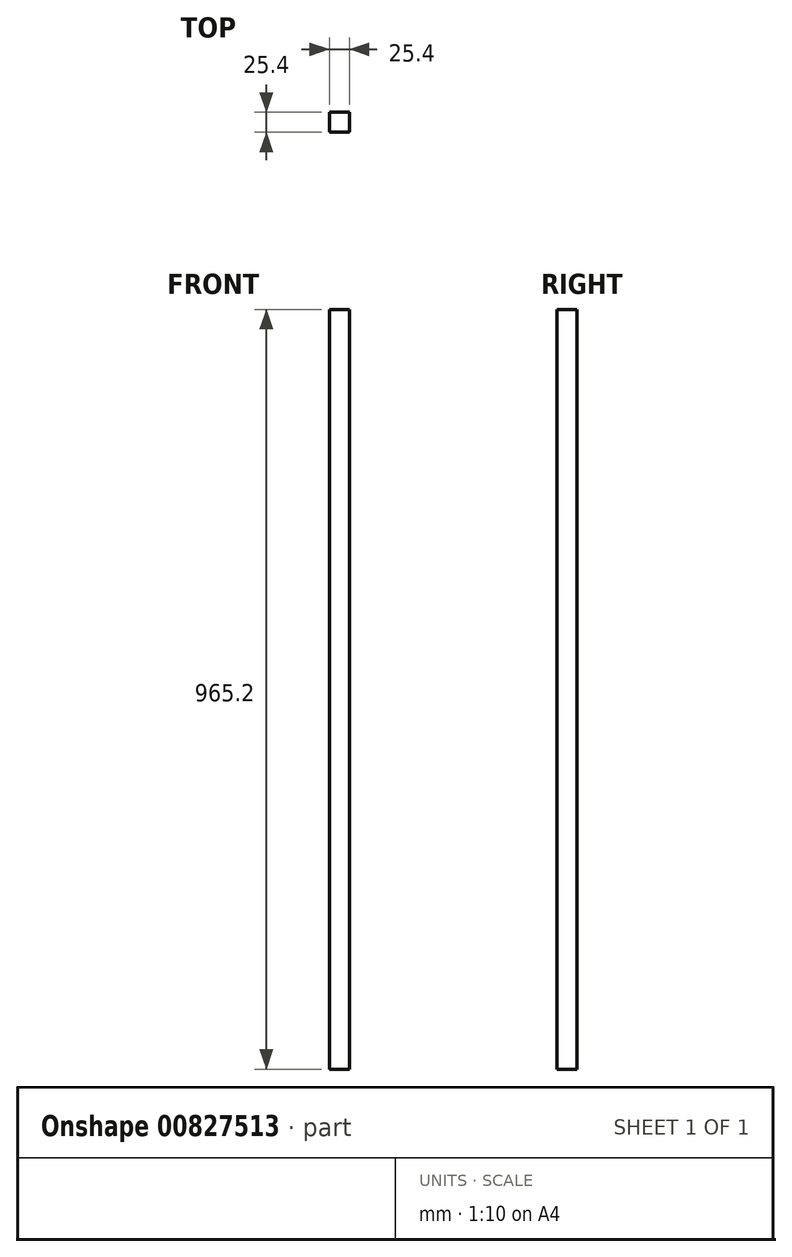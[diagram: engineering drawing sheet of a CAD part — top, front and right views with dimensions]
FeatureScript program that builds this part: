
annotation { "Feature Type Name" : "Feature", "Feature Type Description" : "" }
export const myFeature = defineFeature(function(context is Context, id is Id, definition is map)
    precondition{}
    {
        {
            var Q0;
            Q0=qCreatedBy(makeId("Front.planeOp"),FACE);
            var sketch = newSketch(context, id + "F0", { "sketchPlane" : qUnion([Q0])});
            skLineSegment(sketch, "E0", {"start": v(12.7, 482.6) * mm, "end": v(12.7, -482.6) * mm});
            skLineSegment(sketch, "E1", {"start": v(12.7, -482.6) * mm, "end": v(-12.7, -482.6) * mm});
            skLineSegment(sketch, "E2", {"start": v(12.7, 482.6) * mm, "end": v(-12.7, 482.6) * mm});
            skLineSegment(sketch, "E3", {"start": v(-12.7, 482.6) * mm, "end": v(-12.7, -482.6) * mm});
            skSolve(sketch);
        }
        {
            var Q0;
            Q0=makeQuery(id+"F0.imprint","IMPRINT",FACE,{"disambiguationData":[TD([[makeQuery(id+"F0.imprint","IMPRINT",EDGE,{"derivedFrom":sQuery(id+"F0.wireOp",EDGE,"E0")}),-1.0]])]});
            extrude(context, id + "F1", {"entities" : qUnion([Q0]), "depth" : 25.4 * mm, "offsetDistance" : 25.4 * mm});
        }
    });
